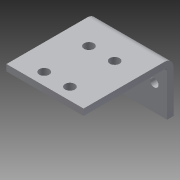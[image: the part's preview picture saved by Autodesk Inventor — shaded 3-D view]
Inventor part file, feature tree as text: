
AUTODESK INVENTOR PART (.ipt)
format: ipt  version: 2014 (Build 180170000, 170)  size: 128,512 bytes
history: native  units: in
note: dims shown in document units (in); Inventor stores cm internally (conversion verified against a paired STEP export)
features: sheet_metal_op x4, sketch x3, other x3
ambient origin geometry x8: Origin, YZ Plane, XZ Plane, XY Plane, X Axis, Y Axis, Z Axis, Center Point
bodies: Solid1 (feature_tree)
feature tree (10):
  sheet_metal_op  "Face1"
  sheet_metal_op  "Flange1"
  sketch  "Sketch1"  dims[d0=1.5in]
  other  "Plate1"
  sketch  "Sketch2"  dims[d1=1.0in]
  other  "Plate2"
  sheet_metal_op  "Bend1"
  sheet_metal_op  "Corner1"
  sketch  "Sketch3"  dims[d2=0.163in d3=0.5in d4=0.25in d5=0.7874in d7=1.0in d8=0.3937in d10=1.0in d12=0.125in d13=0.125in d14=0.0625in d15=0.25in d16=0.125in d17=1.75in d18=90.0deg d19=0.05in d20=0.5in d21=0.125in d22=0.125in d23=0.75in d24=1.31in d25=0.22in d26=0.125in d27=0.19in d28=0.375in d29=0.25in d30=0.125in d31=0.0in]
  other  "Cut1"
